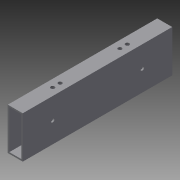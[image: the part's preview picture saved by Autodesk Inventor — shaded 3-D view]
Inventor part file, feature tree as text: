
AUTODESK INVENTOR PART (.ipt)
format: ipt  version: 2015 (Build 190159000, 159)  size: 116,736 bytes
history: native  units: in
note: dims shown in document units (in); Inventor stores cm internally (conversion verified against a paired STEP export)
features: sketch x4, hole x3, extrude x1, projected_geometry x1
ambient origin geometry x8: Origin, YZ Plane, XZ Plane, XY Plane, X Axis, Y Axis, Z Axis, Center Point
bodies: Solid1 (feature_tree)
feature tree (9):
  extrude  "Extrusion1"  Depth=0.5in
  hole  "Hole1"  [1 undecoded]
  hole  "Hole3"  [1 undecoded]
  hole  "Hole4"  [1 undecoded]
  sketch  "Sketch1"  dims[d0=1.4in d1=0.5in]
  sketch  "Sketch2"  dims[d2=0.05in d3=5.0in d4=0.0in]
  sketch  "Sketch4"  dims[d5=0.7in d6=1.0in]
  projected_geometry  "Projected Loop1"
  sketch  "Sketch5"  dims[d7=1.0in d11=0.1285in d12=0.75in d13=0.375in d14=0.25in d15=0.5635in d16=1.0in d17=0.8108in d27=0.25in d28=1.25in d29=1.25in d30=0.128in d31=0.75in d32=0.375in d33=0.25in d34=0.5635in d35=1.0in d36=0.8108in d37=2.5in d38=1.0in d39=1.0in d40=0.25in d41=0.125in d42=0.75in d43=0.375in d44=0.25in d45=0.5635in d46=1.0in d47=0.8108in]
note: 3 required parameter values undecoded (feature->parameter linkage not recoverable at this tier; creation-order binding heuristic only, values carry confidence <= 0.55)
